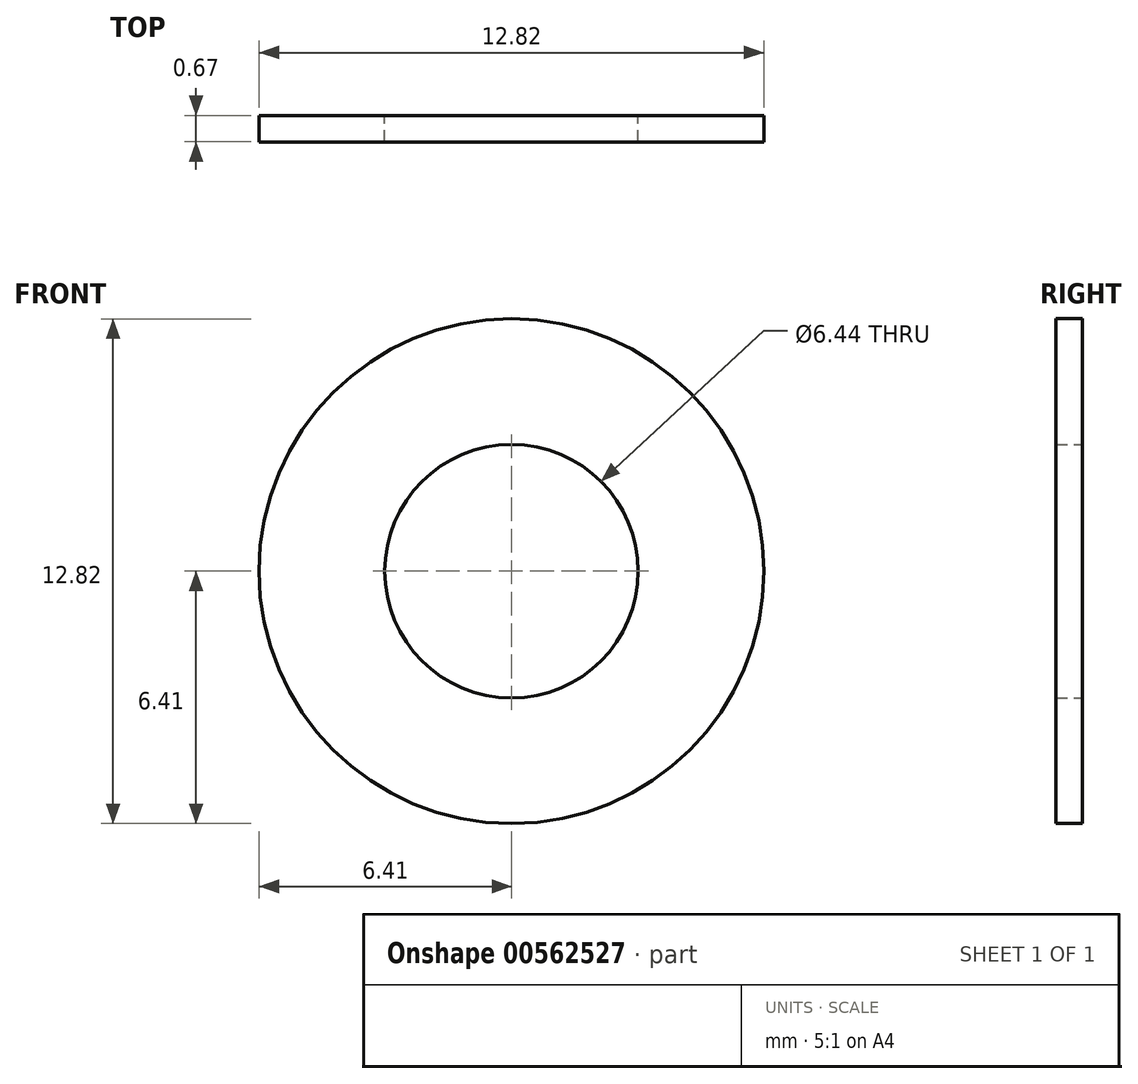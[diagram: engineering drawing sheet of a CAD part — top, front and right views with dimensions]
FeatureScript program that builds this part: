
annotation { "Feature Type Name" : "Feature", "Feature Type Description" : "" }
export const myFeature = defineFeature(function(context is Context, id is Id, definition is map)
    precondition{}
    {
        {
            var Q0;
            Q0=qCreatedBy(makeId("Front.planeOp"),FACE);
            var sketch = newSketch(context, id + "F0", { "sketchPlane" : qUnion([Q0])});
            skCircle(sketch, "E0", {"center": v(0, 0) * mm, "radius": 6.41 * mm});
            skCircle(sketch, "E1", {"center": v(0, 0) * mm, "radius": 3.22 * mm});
            skSolve(sketch);
        }
        {
            var Q0;
            Q0 = qSketchRegion(id + "F0", true);
            extrude(context, id + "F1", {"entities" : qUnion([Q0]), "depth" : 0.67 * mm, "offsetDistance" : 25.4 * mm});
        }
    });
